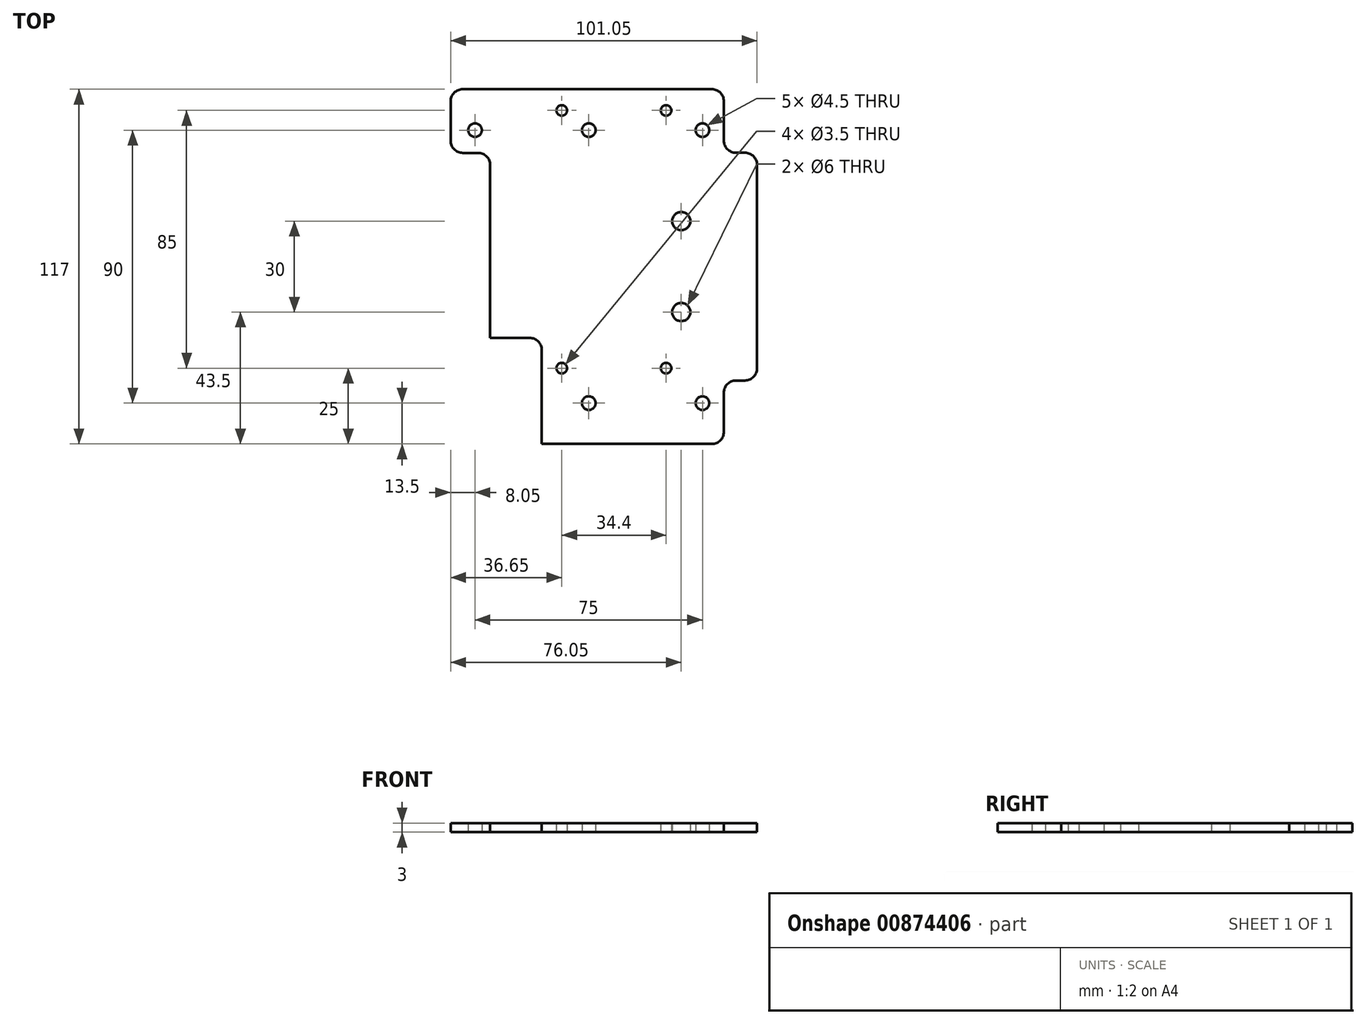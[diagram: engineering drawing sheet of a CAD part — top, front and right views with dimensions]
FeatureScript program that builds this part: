
annotation { "Feature Type Name" : "Feature", "Feature Type Description" : "" }
export const myFeature = defineFeature(function(context is Context, id is Id, definition is map)
    precondition{}
    {
        {
            var Q0;
            Q0=qCreatedBy(makeId("Top.planeOp"),FACE);
            var sketch = newSketch(context, id + "F0", { "sketchPlane" : qUnion([Q0])});
            skLineSegment(sketch, "E0.bottom", {"start": v(-60.5, 60.5) * mm, "end": v(60.5, 60.5) * mm});
            skLineSegment(sketch, "E0.top", {"start": v(-60.5, -60.5) * mm, "end": v(60.5, -60.5) * mm});
            skLineSegment(sketch, "E0.left", {"start": v(-60.5, 60.5) * mm, "end": v(-60.5, -60.5) * mm});
            skLineSegment(sketch, "E0.right", {"start": v(60.5, 60.5) * mm, "end": v(60.5, -60.5) * mm});
            skLineSegment(sketch, "E1.bottom", {"start": v(60.5, 60.5) * mm, "end": v(47.55, 60.5) * mm});
            skLineSegment(sketch, "E1.top", {"start": v(60.5, 47.55) * mm, "end": v(47.55, 47.55) * mm});
            skLineSegment(sketch, "E1.left", {"start": v(60.5, 60.5) * mm, "end": v(60.5, 47.55) * mm});
            skLineSegment(sketch, "E1.right", {"start": v(47.55, 60.5) * mm, "end": v(47.55, 47.55) * mm});
            skLineSegment(sketch, "E2.MirrorCS", {"start": v(-60.5, 47.55) * mm, "end": v(-47.55, 47.55) * mm});
            skLineSegment(sketch, "E3.MirrorCS", {"start": v(-47.55, 60.5) * mm, "end": v(-47.55, 47.55) * mm});
            skLineSegment(sketch, "E4.MirrorCS", {"start": v(-60.5, 60.5) * mm, "end": v(-60.5, 47.55) * mm});
            skLineSegment(sketch, "E5.MirrorCS", {"start": v(-60.5, 60.5) * mm, "end": v(-47.55, 60.5) * mm});
            skLineSegment(sketch, "E6.MirrorCS", {"start": v(60.5, 60.5) * mm, "end": v(-60.5, 60.5) * mm});
            skLineSegment(sketch, "E7.MirrorCS", {"start": v(60.5, -47.55) * mm, "end": v(47.55, -47.55) * mm});
            skLineSegment(sketch, "E8.MirrorCS", {"start": v(47.55, -60.5) * mm, "end": v(47.55, -47.55) * mm});
            skLineSegment(sketch, "E9.MirrorCS", {"start": v(-47.55, -60.5) * mm, "end": v(-47.55, -47.55) * mm});
            skLineSegment(sketch, "E10.MirrorCS", {"start": v(-60.5, -47.55) * mm, "end": v(-47.55, -47.55) * mm});
            skCircle(sketch, "E11", {"center": v(0, 45) * mm, "radius": 2.25 * mm});
            skCircle(sketch, "E12", {"center": v(37.5, 45) * mm, "radius": 2.25 * mm});
            skCircle(sketch, "E13", {"center": v(45, 0) * mm, "radius": 2.25 * mm});
            skCircle(sketch, "E14.MirrorC", {"center": v(-37.5, 45) * mm, "radius": 2.25 * mm});
            skCircle(sketch, "E15.MirrorC", {"center": v(0, -45) * mm, "radius": 2.25 * mm});
            skCircle(sketch, "E16.MirrorC", {"center": v(37.5, -45) * mm, "radius": 2.25 * mm});
            skCircle(sketch, "E17.MirrorC", {"center": v(-37.5, -45) * mm, "radius": 2.25 * mm});
            skCircle(sketch, "E18.MirrorC", {"center": v(-45, 0) * mm, "radius": 2.25 * mm});
            skSolve(sketch);
        }
        {
            var Q0;
            Q0=qCreatedBy(makeId("Top.planeOp"),FACE);
            var sketch = newSketch(context, id + "F1", { "sketchPlane" : qUnion([Q0])});
            skLineSegment(sketch, "E19.bottom", {"start": v(-32.5, 58.5) * mm, "end": v(44.55, 58.5) * mm});
            skLineSegment(sketch, "E19.top", {"start": v(-32.5, -58.5) * mm, "end": v(44.55, -58.5) * mm});
            skLineSegment(sketch, "E19.left", {"start": v(-32.5, 37.5) * mm, "end": v(-32.5, 0) * mm});
            skLineSegment(sketch, "E19.right", {"start": v(44.55, 58.5) * mm, "end": v(44.55, 37.55) * mm});
            skCircle(sketch, "E20.0", {"center": v(37.5, 45) * mm, "radius": 2.25 * mm});
            skCircle(sketch, "E21.0", {"center": v(37.5, -45) * mm, "radius": 2.25 * mm});
            skCircle(sketch, "E22.0", {"center": v(0, -45) * mm, "radius": 2.25 * mm});
            skCircle(sketch, "E23.0", {"center": v(0, 45) * mm, "radius": 2.25 * mm});
            skCircle(sketch, "E24.0", {"center": v(-37.5, 45) * mm, "radius": 2.25 * mm});
            skLineSegment(sketch, "E25", {"start": v(-32.5, 58.5) * mm, "end": v(-45.55, 58.5) * mm});
            skLineSegment(sketch, "E26", {"start": v(-45.55, 58.5) * mm, "end": v(-45.55, 37.5) * mm});
            skLineSegment(sketch, "E27", {"start": v(-45.55, 37.5) * mm, "end": v(-32.5, 37.5) * mm});
            skLineSegment(sketch, "E28.bottom", {"start": v(-8.9, 51.5) * mm, "end": v(25.5, 51.5) * mm, "construction": true});
            skLineSegment(sketch, "E28.top", {"start": v(-8.9, -33.5) * mm, "end": v(25.5, -33.5) * mm, "construction": true});
            skLineSegment(sketch, "E28.left", {"start": v(-8.9, 51.5) * mm, "end": v(-8.9, -33.5) * mm, "construction": true});
            skLineSegment(sketch, "E28.right", {"start": v(25.5, 51.5) * mm, "end": v(25.5, -33.5) * mm, "construction": true});
            skLineSegment(sketch, "E29", {"start": v(44.55, 37.55) * mm, "end": v(55.5, 37.55) * mm});
            skLineSegment(sketch, "E30", {"start": v(55.5, 37.55) * mm, "end": v(55.5, -37.55) * mm});
            skLineSegment(sketch, "E31", {"start": v(55.5, -37.55) * mm, "end": v(44.55, -37.55) * mm});
            skLineSegment(sketch, "E32.trimOffspring", {"start": v(44.55, -37.55) * mm, "end": v(44.55, -58.5) * mm});
            skCircle(sketch, "E33", {"center": v(-8.9, 51.5) * mm, "radius": 1.75 * mm});
            skCircle(sketch, "E34", {"center": v(25.5, 51.5) * mm, "radius": 1.75 * mm});
            skCircle(sketch, "E35", {"center": v(-8.9, -33.5) * mm, "radius": 1.75 * mm});
            skCircle(sketch, "E36", {"center": v(25.5, -33.5) * mm, "radius": 1.75 * mm});
            skCircle(sketch, "E37", {"center": v(30.5, 15) * mm, "radius": 3 * mm});
            skCircle(sketch, "E38", {"center": v(30.5, -15) * mm, "radius": 3 * mm});
            skLineSegment(sketch, "E39.trimOffspring", {"start": v(-32.5, 0) * mm, "end": v(-32.5, -58.5) * mm});
            skSolve(sketch);
        }
        {
            var Q0;
            Q0 = qSketchRegion(id + "F1", true);
            extrude(context, id + "F2", {"entities" : qUnion([Q0]), "depth" : 3 * mm, "offsetDistance" : 25 * mm});
        }
        {
            var Q0;
            Q0=qCreatedBy(makeId("Top.planeOp"),FACE);
            var sketch = newSketch(context, id + "F3", { "sketchPlane" : qUnion([Q0])});
            skLineSegment(sketch, "E40.bottom", {"start": v(-32.5, -23.5) * mm, "end": v(-15.5, -23.5) * mm});
            skLineSegment(sketch, "E40.top", {"start": v(-32.5, -58.5) * mm, "end": v(-15.5, -58.5) * mm});
            skLineSegment(sketch, "E40.left", {"start": v(-32.5, -23.5) * mm, "end": v(-32.5, -58.5) * mm});
            skLineSegment(sketch, "E40.right", {"start": v(-15.5, -23.5) * mm, "end": v(-15.5, -58.5) * mm});
            skSolve(sketch);
        }
        {
            var Q0;
            Q0 = qSketchRegion(id + "F3", true);
            extrude(context, id + "F4", {"entities" : qUnion([Q0]), "operationType" : NewBodyOperationType.REMOVE, "endBound" : BoundingType.THROUGH_ALL, "depth" : 25 * mm, "offsetDistance" : 25 * mm});
        }
        {
            var Q0;
            Q0=makeQuery(id+"F2.opExtrude","SWEPT_EDGE",EDGE,{"disambiguationData":[OSD([sQuery(id+"F1.wireOp",EDGE,"E26"),sQuery(id+"F1.wireOp",EDGE,"E27")])]});
            var Q1;
            Q1=makeQuery(id+"F2.opExtrude","SWEPT_EDGE",EDGE,{"disambiguationData":[OSD([sQuery(id+"F1.wireOp",EDGE,"E25"),sQuery(id+"F1.wireOp",EDGE,"E26")])]});
            var Q2;
            Q2=makeQuery(id+"F2.opExtrude","SWEPT_EDGE",EDGE,{"disambiguationData":[OSD([sQuery(id+"F1.wireOp",EDGE,"E19.left"),sQuery(id+"F1.wireOp",EDGE,"1ZTdFMWL-S7Ej-3sK0-6CI1-nkISHzymhy9g")])]});
            var Q3;
            Q3=makeQuery(id+"F4.boolean.opBoolean","COPY",EDGE,{"derivedFrom":makeQuery(id+"F4.opExtrude","SWEPT_EDGE",EDGE,{"disambiguationData":[OSD([sQuery(id+"F3.wireOp",EDGE,"E40.bottom"),sQuery(id+"F3.wireOp",EDGE,"E40.left")])]})});
            var Q4;
            Q4=makeQuery(id+"F2.opExtrude","SWEPT_EDGE",EDGE,{"disambiguationData":[OSD([sQuery(id+"F1.wireOp",EDGE,"hBK1U4SA-Ncoj-n7go-4rAh-ZTO9ih4BXUu4"),sQuery(id+"F1.wireOp",EDGE,"E39.trimOffspring")])]});
            var Q5;
            Q5=makeQuery(id+"F4.boolean.opBoolean","COPY",EDGE,{"derivedFrom":makeQuery(id+"F4.opExtrude","SWEPT_EDGE",EDGE,{"disambiguationData":[OSD([sQuery(id+"F3.wireOp",EDGE,"E40.top"),sQuery(id+"F3.wireOp",EDGE,"E40.right")])]})});
            var Q6;
            Q6=makeQuery(id+"F4.boolean.opBoolean","COPY",EDGE,{"derivedFrom":makeQuery(id+"F4.opExtrude","SWEPT_EDGE",EDGE,{"disambiguationData":[OSD([sQuery(id+"F3.wireOp",EDGE,"E40.bottom"),sQuery(id+"F3.wireOp",EDGE,"E40.right")])]})});
            var Q7;
            Q7=makeQuery(id+"F2.opExtrude","SWEPT_EDGE",EDGE,{"disambiguationData":[OSD([sQuery(id+"F1.wireOp",EDGE,"E19.top"),sQuery(id+"F1.wireOp",EDGE,"E32.trimOffspring")])]});
            var Q8;
            Q8=makeQuery(id+"F2.opExtrude","SWEPT_EDGE",EDGE,{"disambiguationData":[OSD([sQuery(id+"F1.wireOp",EDGE,"E31"),sQuery(id+"F1.wireOp",EDGE,"E32.trimOffspring")])]});
            var Q9;
            Q9=makeQuery(id+"F2.opExtrude","SWEPT_EDGE",EDGE,{"disambiguationData":[OSD([sQuery(id+"F1.wireOp",EDGE,"E30"),sQuery(id+"F1.wireOp",EDGE,"E31")])]});
            var Q10;
            Q10=makeQuery(id+"F2.opExtrude","SWEPT_EDGE",EDGE,{"disambiguationData":[OSD([sQuery(id+"F1.wireOp",EDGE,"E29"),sQuery(id+"F1.wireOp",EDGE,"E30")])]});
            var Q11;
            Q11=makeQuery(id+"F2.opExtrude","SWEPT_EDGE",EDGE,{"disambiguationData":[OSD([sQuery(id+"F1.wireOp",EDGE,"E19.right"),sQuery(id+"F1.wireOp",EDGE,"E29")])]});
            var Q12;
            Q12=makeQuery(id+"F2.opExtrude","SWEPT_EDGE",EDGE,{"disambiguationData":[OSD([sQuery(id+"F1.wireOp",EDGE,"E19.bottom"),sQuery(id+"F1.wireOp",EDGE,"E19.right")])]});
            fillet(context, id + "F5", {"entities" : qUnion([Q0, Q1, Q2, Q3, Q4, Q5, Q6, Q7, Q8, Q9, Q10, Q11, Q12]), "radius" : 4 * mm, "tangentPropagation" : true, "allowEdgeOverflow" : false});
        }
    });
